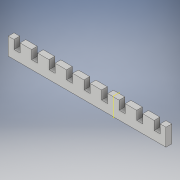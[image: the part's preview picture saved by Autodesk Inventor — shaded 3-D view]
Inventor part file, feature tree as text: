
AUTODESK INVENTOR PART (.ipt)
format: ipt  version: 2017 (Build 210142000, 142)  size: 148,992 bytes
history: native  units: in
note: dims shown in document units (in); Inventor stores cm internally (conversion verified against a paired STEP export)
features: mirror x5, extrude x1, plane x1, sketch x1
ambient origin geometry x8: Origin, YZ Plane, XZ Plane, XY Plane, X Axis, Y Axis, Z Axis, Center Point
bodies: Solid1 (feature_tree)
feature tree (8):
  extrude  "Extrusion1"  Depth=0.2047in
  mirror  "Mirror1"
  mirror  "Mirror2"
  mirror  "Mirror4"
  mirror  "Mirror5"
  plane  "Work Plane3"
  mirror  "Mirror7"
  sketch  "Sketch1"  dims[d0=0.5906in d1=0.2047in d2=0.1969in d3=0.1969in d4=0.2953in d5=0.1969in d6=0.0in]
